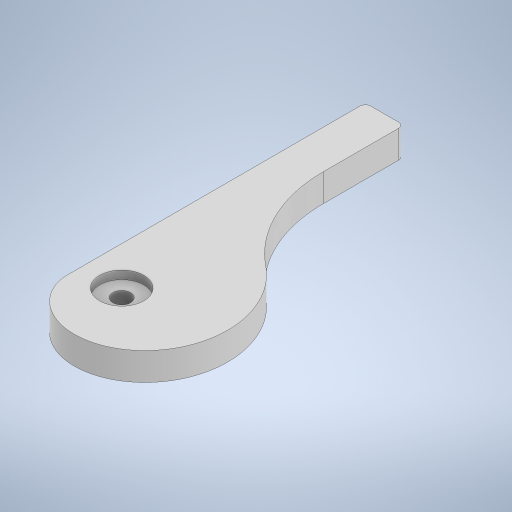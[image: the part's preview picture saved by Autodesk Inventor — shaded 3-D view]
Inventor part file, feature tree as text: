
AUTODESK INVENTOR PART (.ipt)
format: ipt  version: 2023 (Build 270158000, 158)  size: 266,240 bytes
history: native  units: mm
features: extrude x2, sketch x2, fillet x1, other x1
ambient origin geometry x8: Origin, YZ Plane, XZ Plane, XY Plane, X Axis, Y Axis, Z Axis, Center Point
bodies: Solid1 (feature_tree)
feature tree (6):
  extrude  "Extrusion1"  Depth=12.7mm
  fillet  "Fillet1"  Radius=6.35mm
  extrude  "Extrusion2"  Depth=3.0mm
  sketch  "Sketch2"  dims[d2=0.0mm d3=2700.0mm d6=12.7mm d9=6.35mm]
  other  "2D Equation Curve2"
  sketch  "Sketch3"  dims[d10=150.0deg d12=125.0mm d13=10.0mm d14=0.0mm d15=2.0mm d16=16.0mm d17=3.0mm d18=0.0mm]
